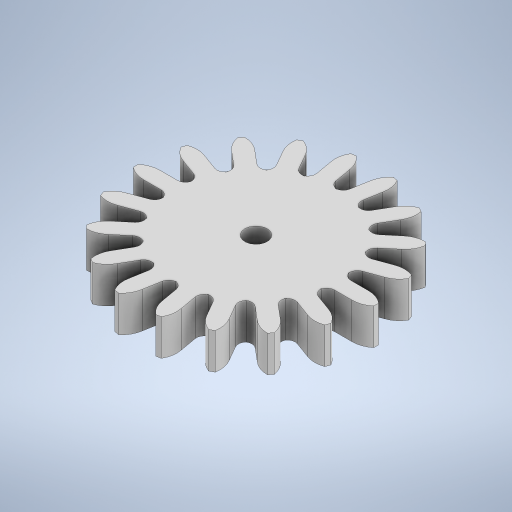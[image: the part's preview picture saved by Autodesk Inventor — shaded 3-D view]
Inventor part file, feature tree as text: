
AUTODESK INVENTOR PART (.ipt)
format: ipt  version: 2024 (Build 280153020, 153B)  size: 496,128 bytes
history: native  units: mm
features: extrude x1, sketch x1
ambient origin geometry x8: Origin, YZ Plane, XZ Plane, XY Plane, X Axis, Y Axis, Z Axis, Center Point
bodies: Solid1 (feature_tree)
feature tree (2):
  extrude  "Extrusion1"  Depth=4.5mm
  sketch  "Sketch1"  dims[d0=2.8mm d1=20.0mm d4=1.570796mm d5=0.785398mm d6=3.0mm d7=0.3mm d8=0.6mm d9=3.0mm d11=1.0mm d12=1.0mm d13=180.0mm d15=360.0deg d17=4.5mm d18=0.0mm]
